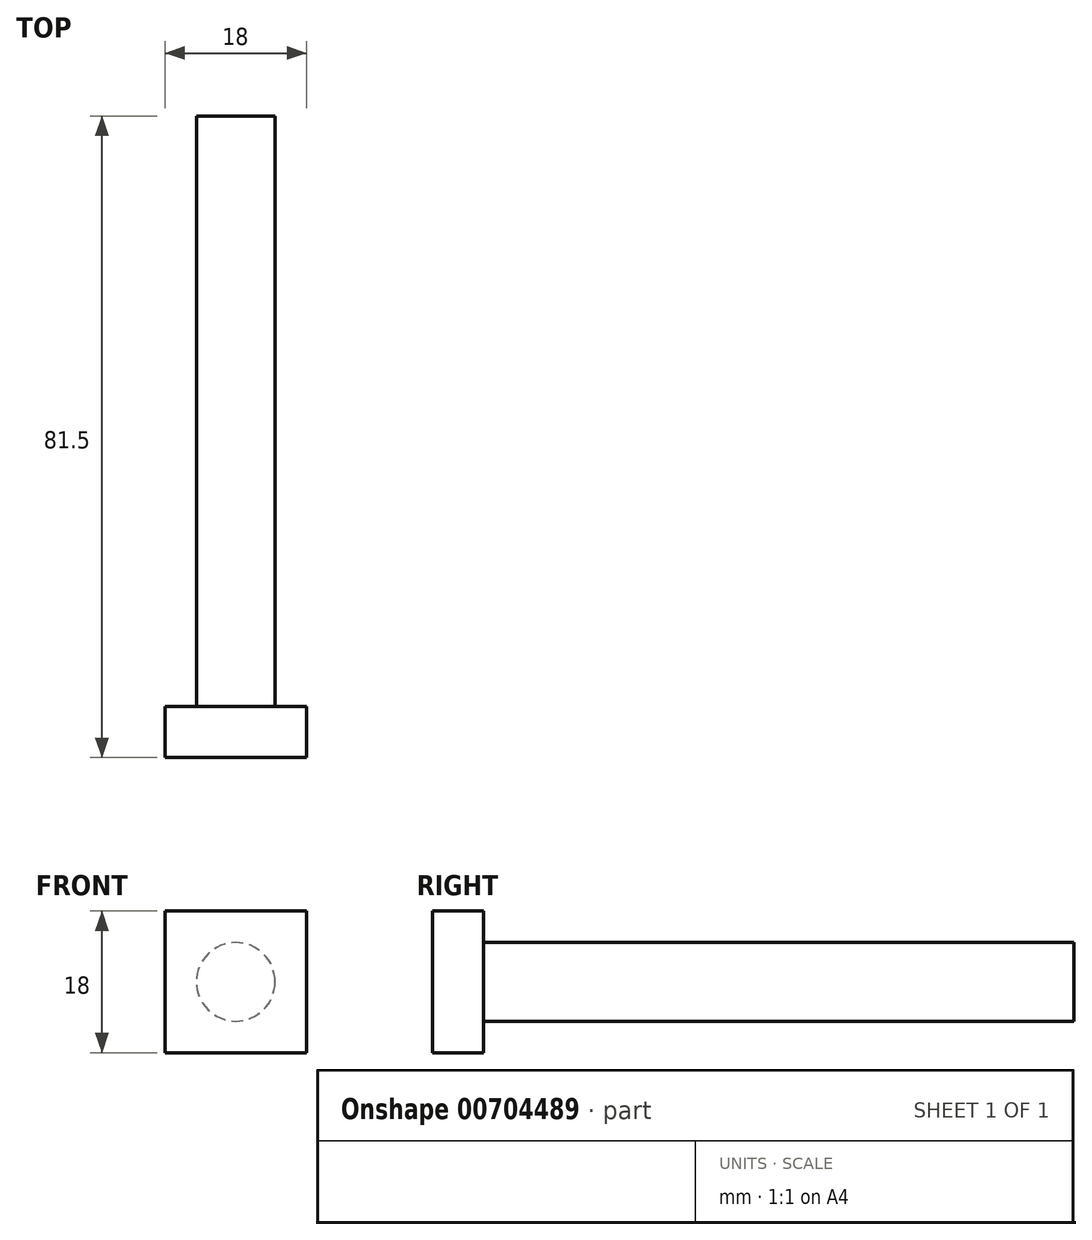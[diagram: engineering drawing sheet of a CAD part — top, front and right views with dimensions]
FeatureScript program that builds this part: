
annotation { "Feature Type Name" : "Feature", "Feature Type Description" : "" }
export const myFeature = defineFeature(function(context is Context, id is Id, definition is map)
    precondition{}
    {
        {
            var Q0;
            Q0=qCreatedBy(makeId("Front.planeOp"),FACE);
            var sketch = newSketch(context, id + "F0", { "sketchPlane" : qUnion([Q0])});
            skLineSegment(sketch, "E0.bottom", {"start": v(9, 9) * mm, "end": v(-9, 9) * mm});
            skLineSegment(sketch, "E0.top", {"start": v(9, -9) * mm, "end": v(-9, -9) * mm});
            skLineSegment(sketch, "E0.left", {"start": v(9, 9) * mm, "end": v(9, -9) * mm});
            skLineSegment(sketch, "E0.right", {"start": v(-9, 9) * mm, "end": v(-9, -9) * mm});
            skPoint(sketch, "E0.middle", {"position": v(0, 0) * mm});
            skSolve(sketch);
        }
        {
            var Q0;
            Q0=qSketchRegion(id+"F0",true);
            extrude(context, id + "F1", {"entities" : qUnion([Q0]), "depth" : 6.5 * mm, "offsetDistance" : 25 * mm});
        }
        {
            var Q0;
            Q0=makeQuery(id+"F1.opExtrude","CAP_FACE",FACE,{"disambiguationData":[OSD([sQuery(id+"F0.wireOp",EDGE,"E0.bottom"),sQuery(id+"F0.wireOp",EDGE,"E0.top"),sQuery(id+"F0.wireOp",EDGE,"E0.left"),sQuery(id+"F0.wireOp",EDGE,"E0.right")])],"isStart":true});
            var sketch = newSketch(context, id + "F2", { "sketchPlane" : qUnion([Q0])});
            skCircle(sketch, "E1", {"center": v(0, 0) * mm, "radius": 5 * mm});
            skSolve(sketch);
        }
        {
            var Q0;
            Q0=qSketchRegion(id+"F2",true);
            extrude(context, id + "F3", {"entities" : qUnion([Q0]), "operationType" : NewBodyOperationType.ADD, "depth" : 75 * mm, "offsetDistance" : 25 * mm});
        }
    });
